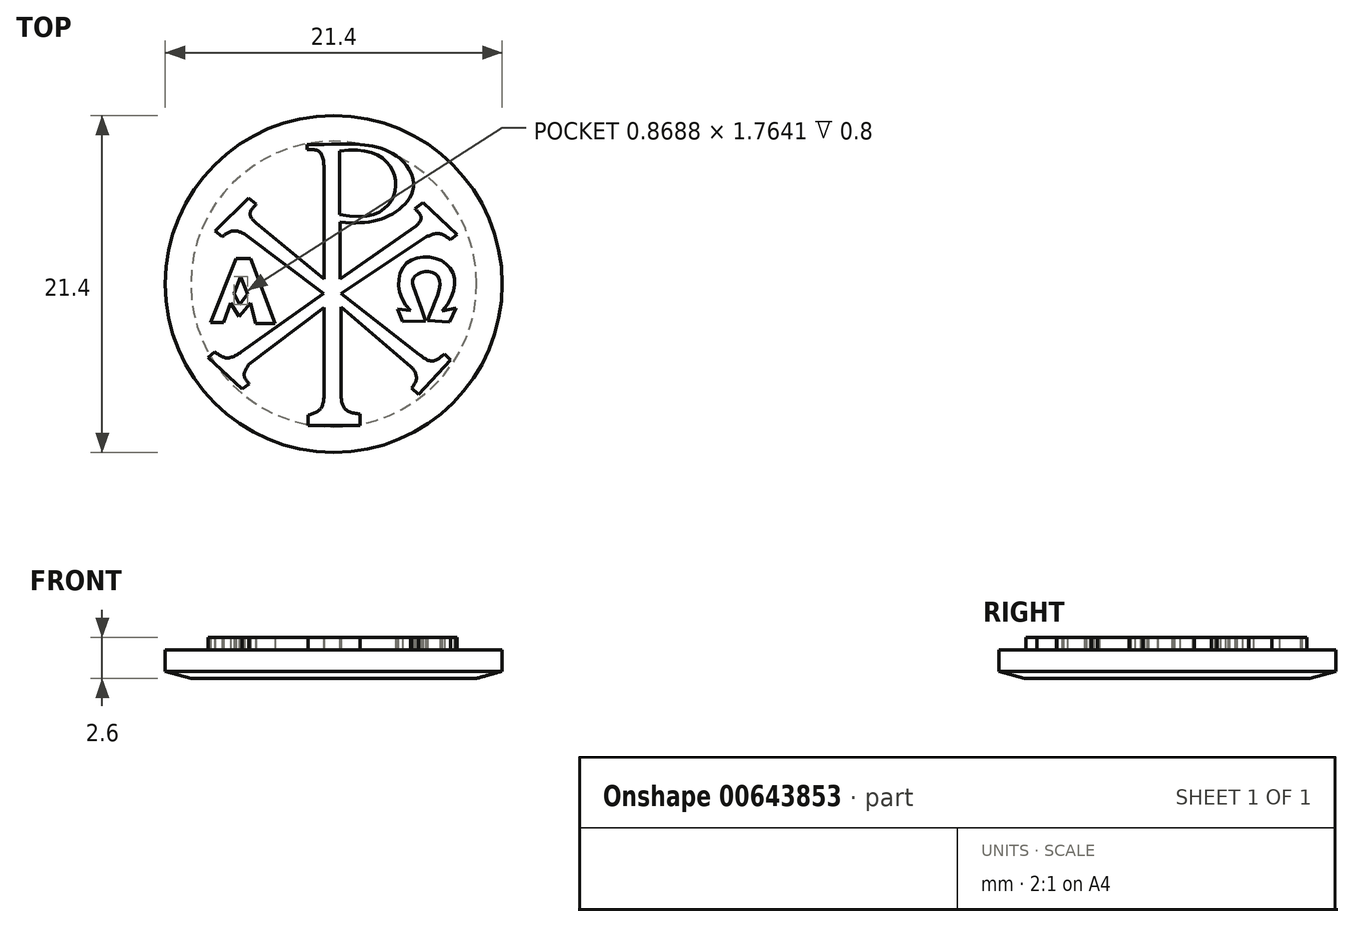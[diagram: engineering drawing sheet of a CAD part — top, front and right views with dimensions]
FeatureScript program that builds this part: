
annotation { "Feature Type Name" : "Feature", "Feature Type Description" : "" }
export const myFeature = defineFeature(function(context is Context, id is Id, definition is map)
    precondition{}
    {
        {
            var Q0;
            Q0=qCreatedBy(makeId("Front.planeOp"),FACE);
            var sketch = newSketch(context, id + "F0", { "sketchPlane" : qUnion([Q0])});
            skLineSegment(sketch, "E0", {"start": v(-10.7, 1.8) * mm, "end": v(0, 1.8) * mm});
            skLineSegment(sketch, "E1", {"start": v(-10.7, 1.8) * mm, "end": v(-10.7, 0.45) * mm});
            skLineSegment(sketch, "E2", {"start": v(-9.07, 0) * mm, "end": v(0, 0) * mm});
            skLineSegment(sketch, "E3", {"start": v(-10.7, 0.45) * mm, "end": v(-9.07, 0) * mm});
            skLineSegment(sketch, "E4", {"start": v(0, 0) * mm, "end": v(0, 1.8) * mm});
            skLineSegment(sketch, "E5", {"start": v(0, 2.4) * mm, "end": v(0, 0) * mm, "construction": true});
            skSolve(sketch);
        }
        {
            var Q0;
            Q0=qSketchRegion(id+"F0",true);
            var Q1;
            Q1=sQuery(id+"F0.wireOp",EDGE,"E5");
            revolve(context, id + "F1", {"entities" : qUnion([Q0]), "axis" : qUnion([Q1]), "revolveType" : RevolveType.FULL});
        }
        {
            var Q0;
            Q0=makeQuery(id+"F1.opRevolve","SWEPT_FACE",FACE,{"disambiguationData":[OSD([sQuery(id+"F0.wireOp",EDGE,"E0")])]});
            var sketch = newSketch(context, id + "F2", { "sketchPlane" : qUnion([Q0])});
            skFitSpline(sketch, "E6", {"points": [v(-1.69, 8.85) * mm, v(2.95, 8.63) * mm, v(5.05, 6.65) * mm], "startDerivative": vector(13.65, 0.13) * mm, "endDerivative": vector(2.25, -7.82) * mm});
            skFitSpline(sketch, "E7", {"points": [v(5.05, 6.65) * mm, v(3.84, 4.52) * mm, v(0.4, 3.94) * mm], "startDerivative": vector(1.13, -5.98) * mm, "endDerivative": vector(-7.93, 0.87) * mm});
            skFitSpline(sketch, "E8", {"points": [v(0.38, 8.45) * mm, v(3.94, 6.4) * mm, v(0.38, 4.42) * mm], "startDerivative": vector(14.01, 2.35) * mm, "endDerivative": vector(-15.33, 3.52) * mm});
            skLineSegment(sketch, "E9", {"start": v(0.38, 8.45) * mm, "end": v(0.38, 4.42) * mm});
            skLineSegment(sketch, "E10", {"start": v(-1.69, 8.85) * mm, "end": v(-1.69, 8.53) * mm});
            skFitSpline(sketch, "E11", {"points": [v(-1.69, 8.53) * mm, v(-0.9, 8.39) * mm, v(-0.61, 7.13) * mm], "startDerivative": vector(2.1, 0.1) * mm, "endDerivative": vector(0.03, -2.8) * mm});
            skLineSegment(sketch, "E12", {"start": v(-0.61, 7.13) * mm, "end": v(-0.61, 0.32) * mm});
            skLineSegment(sketch, "E13", {"start": v(-4.92, 3.86) * mm, "end": v(-0.61, 0.32) * mm});
            skLineSegment(sketch, "E14", {"start": v(0.4, 3.94) * mm, "end": v(0.4, 0.3) * mm});
            skLineSegment(sketch, "E15", {"start": v(0.4, 0.3) * mm, "end": v(5.24, 3.7) * mm});
            skLineSegment(sketch, "E16", {"start": v(-5.68, 3.17) * mm, "end": v(-0.66, -0.6) * mm});
            skLineSegment(sketch, "E17", {"start": v(-0.66, -0.6) * mm, "end": v(-5.87, -4.33) * mm});
            skLineSegment(sketch, "E18", {"start": v(-5.4, -5.13) * mm, "end": v(-0.61, -1.5) * mm});
            skLineSegment(sketch, "E19", {"start": v(-0.61, -1.5) * mm, "end": v(-0.61, -7.05) * mm});
            skLineSegment(sketch, "E20", {"start": v(0.45, -7.05) * mm, "end": v(0.45, -1.47) * mm});
            skLineSegment(sketch, "E21", {"start": v(0.45, -1.47) * mm, "end": v(4.9, -5.26) * mm});
            skLineSegment(sketch, "E22", {"start": v(5.9, 3) * mm, "end": v(0.46, -0.6) * mm});
            skLineSegment(sketch, "E23", {"start": v(0.46, -0.6) * mm, "end": v(5.43, -4.48) * mm});
            skLineSegment(sketch, "E24", {"start": v(-1.64, -8.33) * mm, "end": v(-1.64, -8.98) * mm});
            skLineSegment(sketch, "E25", {"start": v(-1.64, -8.98) * mm, "end": v(1.67, -8.98) * mm});
            skLineSegment(sketch, "E26", {"start": v(1.67, -8.98) * mm, "end": v(1.67, -8.27) * mm});
            skLineSegment(sketch, "E27", {"start": v(-7.56, -4.32) * mm, "end": v(-7.98, -4.66) * mm});
            skLineSegment(sketch, "E28", {"start": v(-7.98, -4.66) * mm, "end": v(-5.8, -6.68) * mm});
            skLineSegment(sketch, "E29", {"start": v(-5.8, -6.68) * mm, "end": v(-5.38, -6.34) * mm});
            skFitSpline(sketch, "E30", {"points": [v(-5.87, -4.33) * mm, v(-6.78, -4.7) * mm, v(-7.56, -4.32) * mm], "startDerivative": vector(-1.81, -1.1) * mm, "endDerivative": vector(-1.57, 1.15) * mm});
            skFitSpline(sketch, "E31", {"points": [v(-5.4, -5.13) * mm, v(-5.69, -5.77) * mm, v(-5.38, -6.34) * mm], "startDerivative": vector(-0.86, -1.29) * mm, "endDerivative": vector(0.93, -1.14) * mm});
            skLineSegment(sketch, "E32", {"start": v(7.03, -4.45) * mm, "end": v(7.43, -4.82) * mm});
            skLineSegment(sketch, "E33", {"start": v(7.43, -4.82) * mm, "end": v(5.37, -7) * mm});
            skLineSegment(sketch, "E34", {"start": v(5.37, -7) * mm, "end": v(4.95, -6.61) * mm});
            skFitSpline(sketch, "E35", {"points": [v(4.9, -5.26) * mm, v(5.25, -5.97) * mm, v(4.95, -6.61) * mm], "startDerivative": vector(1.23, -0.94) * mm, "endDerivative": vector(-0.93, -1.3) * mm});
            skFitSpline(sketch, "E36", {"points": [v(5.43, -4.48) * mm, v(6.25, -4.9) * mm, v(7.03, -4.45) * mm], "startDerivative": vector(1.65, -1.26) * mm, "endDerivative": vector(1.54, 1.33) * mm});
            skFitSpline(sketch, "E37", {"points": [v(-0.61, -7.05) * mm, v(-0.84, -7.92) * mm, v(-1.64, -8.33) * mm], "startDerivative": vector(-0.16, -1.97) * mm, "endDerivative": vector(-1.9, -0.6) * mm});
            skFitSpline(sketch, "E38", {"points": [v(0.45, -7.05) * mm, v(0.71, -7.93) * mm, v(1.67, -8.27) * mm], "startDerivative": vector(0.2, -2.09) * mm, "endDerivative": vector(2.22, -0.37) * mm});
            skFitSpline(sketch, "E39", {"points": [v(5.16, 4.78) * mm, v(5.56, 4.22) * mm, v(5.24, 3.7) * mm], "startDerivative": vector(1.13, -1.1) * mm, "endDerivative": vector(-1, -1.08) * mm});
            skFitSpline(sketch, "E40", {"points": [v(5.9, 3) * mm, v(6.68, 3.2) * mm, v(7.43, 2.82) * mm], "startDerivative": vector(1.6, 0.68) * mm, "endDerivative": vector(1.46, -1.04) * mm});
            skFitSpline(sketch, "E41", {"points": [v(-7.1, 3) * mm, v(-6.38, 3.37) * mm, v(-5.68, 3.17) * mm], "startDerivative": vector(1.38, 1.02) * mm, "endDerivative": vector(1.46, -0.7) * mm});
            skFitSpline(sketch, "E42", {"points": [v(-4.92, 3.86) * mm, v(-5.31, 4.44) * mm, v(-4.92, 5.07) * mm], "startDerivative": vector(-1.19, 1.17) * mm, "endDerivative": vector(1.18, 1.26) * mm});
            skLineSegment(sketch, "E43", {"start": v(-7.1, 3) * mm, "end": v(-7.55, 3.36) * mm});
            skLineSegment(sketch, "E44", {"start": v(-7.55, 3.36) * mm, "end": v(-5.4, 5.46) * mm});
            skLineSegment(sketch, "E45", {"start": v(-5.4, 5.46) * mm, "end": v(-4.92, 5.07) * mm});
            skLineSegment(sketch, "E46", {"start": v(5.16, 4.78) * mm, "end": v(5.68, 5.18) * mm});
            skLineSegment(sketch, "E47", {"start": v(5.68, 5.18) * mm, "end": v(7.82, 3.14) * mm});
            skLineSegment(sketch, "E48", {"start": v(7.82, 3.14) * mm, "end": v(7.43, 2.82) * mm});
            skLineSegment(sketch, "E49", {"start": v(-7.82, -2.43) * mm, "end": v(-6.2, 1.6) * mm});
            skLineSegment(sketch, "E50", {"start": v(-6.2, 1.6) * mm, "end": v(-5.28, 1.6) * mm});
            skLineSegment(sketch, "E51", {"start": v(-5.28, 1.6) * mm, "end": v(-3.73, -2.5) * mm});
            skLineSegment(sketch, "E52", {"start": v(-3.73, -2.5) * mm, "end": v(-4.97, -2.5) * mm});
            skLineSegment(sketch, "E53", {"start": v(-4.97, -2.5) * mm, "end": v(-5.28, -1.2) * mm});
            skLineSegment(sketch, "E54", {"start": v(-5.28, -1.2) * mm, "end": v(-6.02, -2.06) * mm});
            skLineSegment(sketch, "E55", {"start": v(-6.02, -2.06) * mm, "end": v(-6.55, -1.2) * mm});
            skLineSegment(sketch, "E56", {"start": v(-6.55, -1.2) * mm, "end": v(-6.98, -2.43) * mm});
            skLineSegment(sketch, "E57", {"start": v(-6.98, -2.43) * mm, "end": v(-7.82, -2.43) * mm});
            skLineSegment(sketch, "E58", {"start": v(-5.92, 0.46) * mm, "end": v(-6.34, -0.6) * mm});
            skLineSegment(sketch, "E59", {"start": v(-6.34, -0.6) * mm, "end": v(-5.97, -1.3) * mm});
            skLineSegment(sketch, "E60", {"start": v(-5.97, -1.3) * mm, "end": v(-5.47, -0.62) * mm});
            skLineSegment(sketch, "E61", {"start": v(-5.47, -0.62) * mm, "end": v(-5.92, 0.46) * mm});
            skFitSpline(sketch, "E62", {"points": [v(5.83, -2.34) * mm, v(5.1, 0.43) * mm, v(5.91, 0.8) * mm, v(6.72, 0.28) * mm, v(5.94, -2.32) * mm], "startDerivative": vector(-6.33, 19.41) * mm, "endDerivative": vector(-3.44, -9.2) * mm});
            skFitSpline(sketch, "E63", {"points": [v(4.87, -1.7) * mm, v(4.6, 1.3) * mm, v(7.2, 1.23) * mm, v(6.9, -1.7) * mm], "startDerivative": vector(-8, 7.74) * mm, "endDerivative": vector(-8.67, -9.35) * mm});
            skLineSegment(sketch, "E64", {"start": v(4.87, -1.7) * mm, "end": v(4.06, -1.59) * mm});
            skLineSegment(sketch, "E65", {"start": v(4.06, -1.59) * mm, "end": v(4.36, -2.37) * mm});
            skLineSegment(sketch, "E66", {"start": v(4.36, -2.37) * mm, "end": v(5.83, -2.34) * mm});
            skLineSegment(sketch, "E67", {"start": v(6.9, -1.7) * mm, "end": v(7.77, -1.54) * mm});
            skLineSegment(sketch, "E68", {"start": v(7.77, -1.54) * mm, "end": v(7.35, -2.4) * mm});
            skLineSegment(sketch, "E69", {"start": v(7.35, -2.4) * mm, "end": v(5.94, -2.32) * mm});
            skSolve(sketch);
        }
        {
            var Q0;
            Q0 = qSketchRegion(id + "F2", true);
            extrude(context, id + "F3", {"entities" : qUnion([Q0]), "operationType" : NewBodyOperationType.ADD, "depth" : .80 * mm, "offsetDistance" : 25 * mm});
        }
    });
